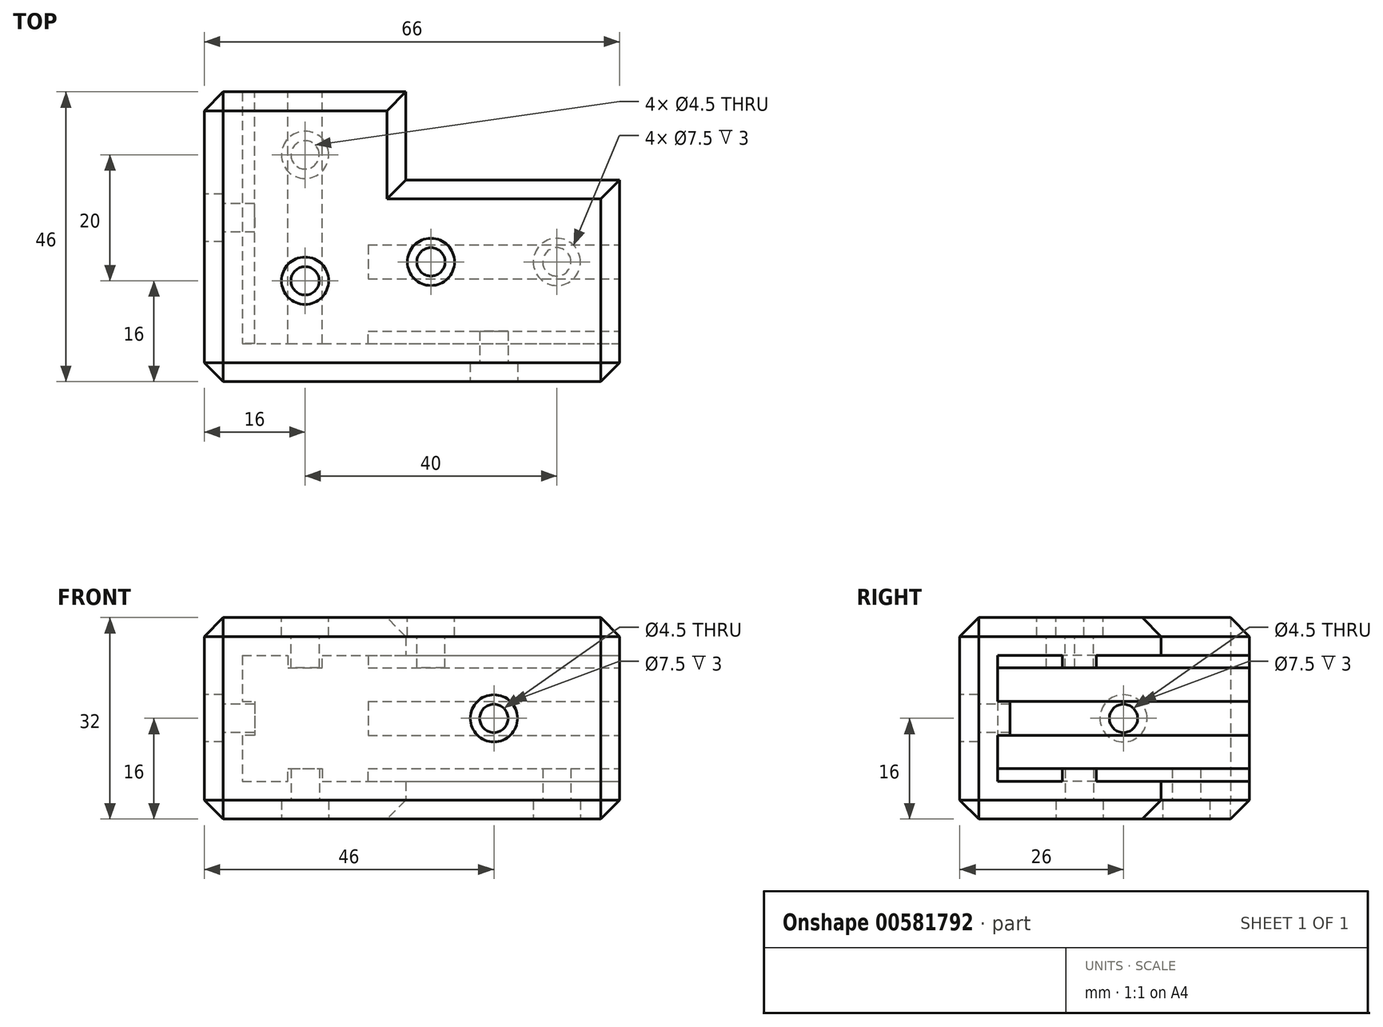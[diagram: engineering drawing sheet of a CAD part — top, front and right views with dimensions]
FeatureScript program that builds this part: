
annotation { "Feature Type Name" : "Feature", "Feature Type Description" : "" }
export const myFeature = defineFeature(function(context is Context, id is Id, definition is map)
    precondition{}
    {
        {
            var Q0;
            Q0=qCreatedBy(makeId("Top.planeOp"),FACE);
            var sketch = newSketch(context, id + "F0", { "sketchPlane" : qUnion([Q0])});
            skLineSegment(sketch, "E0", {"start": v(20, 40) * mm, "end": v(20, 20) * mm, "construction": true});
            skLineSegment(sketch, "E1", {"start": v(20, 20) * mm, "end": v(60, 20) * mm, "construction": true});
            skLineSegment(sketch, "E2", {"start": v(60, 20) * mm, "end": v(60, 0) * mm, "construction": true});
            skLineSegment(sketch, "E3", {"start": v(60, 0) * mm, "end": v(0, 0) * mm, "construction": true});
            skLineSegment(sketch, "E4", {"start": v(0, 0) * mm, "end": v(0, 40) * mm, "construction": true});
            skLineSegment(sketch, "E5", {"start": v(0, 40) * mm, "end": v(20, 40) * mm, "construction": true});
            skLineSegment(sketch, "E6", {"start": v(3.86, 40) * mm, "end": v(26, 40) * mm});
            skLineSegment(sketch, "E7", {"start": v(26, 40) * mm, "end": v(26, 26) * mm});
            skLineSegment(sketch, "E8", {"start": v(26, 26) * mm, "end": v(60, 26) * mm});
            skLineSegment(sketch, "E9", {"start": v(60, 26) * mm, "end": v(60, -6) * mm});
            skLineSegment(sketch, "E10", {"start": v(60, -6) * mm, "end": v(-6, -6) * mm});
            skLineSegment(sketch, "E11", {"start": v(-6, -6) * mm, "end": v(-6, 40) * mm});
            skLineSegment(sketch, "E12", {"start": v(-6, 40) * mm, "end": v(3.86, 40) * mm});
            skSolve(sketch);
        }
        {
            var Q0;
            Q0=qSketchRegion(id+"F0",true);
            extrude(context, id + "F1", {"entities" : qUnion([Q0]), "depth" : 6 * mm});
        }
        {
            var Q0;
            Q0=makeQuery(id+"F1.opExtrude","CAP_FACE",FACE,{"disambiguationData":[OSD([sQuery(id+"F0.wireOp",EDGE,"E6"),sQuery(id+"F0.wireOp",EDGE,"E7"),sQuery(id+"F0.wireOp",EDGE,"E8"),sQuery(id+"F0.wireOp",EDGE,"E9"),sQuery(id+"F0.wireOp",EDGE,"E10"),sQuery(id+"F0.wireOp",EDGE,"E11"),sQuery(id+"F0.wireOp",EDGE,"E12")])],"isStart":false});
            var sketch = newSketch(context, id + "F2", { "sketchPlane" : qUnion([Q0])});
            skLineSegment(sketch, "E13", {"start": v(-6, 40) * mm, "end": v(0, 40) * mm});
            skLineSegment(sketch, "E14", {"start": v(0, 40) * mm, "end": v(0, 0) * mm});
            skLineSegment(sketch, "E15", {"start": v(0, 0) * mm, "end": v(60, 0) * mm});
            skLineSegment(sketch, "E16", {"start": v(60, 0) * mm, "end": v(60, -6) * mm});
            skLineSegment(sketch, "E17", {"start": v(60, -6) * mm, "end": v(-6, -6) * mm});
            skLineSegment(sketch, "E18", {"start": v(-6, -6) * mm, "end": v(-6, 40) * mm});
            skSolve(sketch);
        }
        {
            var Q0;
            Q0=qSketchRegion(id+"F2",true);
            extrude(context, id + "F3", {"entities" : qUnion([Q0]), "operationType" : NewBodyOperationType.ADD, "depth" : 20 * mm});
        }
        {
            var Q0;
            Q0=makeQuery(id+"F3.opExtrude","CAP_FACE",FACE,{"disambiguationData":[OSD([sQuery(id+"F2.wireOp",EDGE,"E13"),sQuery(id+"F2.wireOp",EDGE,"E14"),sQuery(id+"F2.wireOp",EDGE,"E15"),sQuery(id+"F2.wireOp",EDGE,"E16"),sQuery(id+"F2.wireOp",EDGE,"E17"),sQuery(id+"F2.wireOp",EDGE,"E18")])],"isStart":false});
            var sketch = newSketch(context, id + "F4", { "sketchPlane" : qUnion([Q0])});
            skLineSegment(sketch, "E19", {"start": v(-6, -6) * mm, "end": v(-6, 40) * mm});
            skLineSegment(sketch, "E20", {"start": v(-6, 40) * mm, "end": v(26, 40) * mm});
            skLineSegment(sketch, "E21", {"start": v(26, 40) * mm, "end": v(26, 26) * mm});
            skLineSegment(sketch, "E22", {"start": v(26, 26) * mm, "end": v(60, 26) * mm});
            skLineSegment(sketch, "E23", {"start": v(60, 26) * mm, "end": v(60, -6) * mm});
            skLineSegment(sketch, "E24", {"start": v(60, -6) * mm, "end": v(-6, -6) * mm});
            skSolve(sketch);
        }
        {
            var Q0;
            Q0=qSketchRegion(id+"F4",true);
            extrude(context, id + "F5", {"entities" : qUnion([Q0]), "operationType" : NewBodyOperationType.ADD, "depth" : 6 * mm});
        }
        {
            var Q0;
            Q0=makeQuery(id+"F5.boolean.opBoolean","MERGE",FACE,{"derivedFrom":[makeQuery(id+"F3.boolean.opBoolean","MERGE",FACE,{"derivedFrom":[makeQuery(id+"F1.opExtrude","SWEPT_FACE",FACE,{"disambiguationData":[OSD([sQuery(id+"F0.wireOp",EDGE,"E9")])]}),makeQuery(id+"F3.opExtrude","SWEPT_FACE",FACE,{"disambiguationData":[OSD([sQuery(id+"F2.wireOp",EDGE,"E16")])]})]}),makeQuery(id+"F5.opExtrude","SWEPT_FACE",FACE,{"disambiguationData":[OSD([sQuery(id+"F4.wireOp",EDGE,"E23")])]})]});
            var sketch = newSketch(context, id + "F6", { "sketchPlane" : qUnion([Q0])});
            skLineSegment(sketch, "E25", {"start": v(13, 26) * mm, "end": v(10.29, 26) * mm});
            skLineSegment(sketch, "E26", {"start": v(10.29, 26) * mm, "end": v(10.29, 24) * mm});
            skLineSegment(sketch, "E27", {"start": v(10.29, 24) * mm, "end": v(15.7, 24) * mm});
            skLineSegment(sketch, "E28", {"start": v(15.7, 24) * mm, "end": v(15.7, 26) * mm});
            skLineSegment(sketch, "E29", {"start": v(15.7, 26) * mm, "end": v(13, 26) * mm});
            skLineSegment(sketch, "E30", {"start": v(13, 6) * mm, "end": v(10.29, 6) * mm});
            skLineSegment(sketch, "E31", {"start": v(10.29, 6) * mm, "end": v(10.29, 8) * mm});
            skLineSegment(sketch, "E32", {"start": v(10.29, 8) * mm, "end": v(15.7, 8) * mm});
            skLineSegment(sketch, "E33", {"start": v(15.7, 8) * mm, "end": v(15.7, 6) * mm});
            skLineSegment(sketch, "E34", {"start": v(15.7, 6) * mm, "end": v(13, 6) * mm});
            skLineSegment(sketch, "E35", {"start": v(0, 16) * mm, "end": v(0, 18.7) * mm});
            skLineSegment(sketch, "E36", {"start": v(0, 18.7) * mm, "end": v(2, 18.7) * mm});
            skLineSegment(sketch, "E37", {"start": v(2, 18.7) * mm, "end": v(2, 13.29) * mm});
            skLineSegment(sketch, "E38", {"start": v(2, 13.29) * mm, "end": v(0, 13.29) * mm});
            skLineSegment(sketch, "E39", {"start": v(0, 13.29) * mm, "end": v(0, 16) * mm});
            skSolve(sketch);
        }
        {
            var Q0;
            Q0=qSketchRegion(id+"F6",true);
            extrude(context, id + "F7", {"entities" : qUnion([Q0]), "operationType" : NewBodyOperationType.ADD, "oppositeDirection" : true, "depth" : 40 * mm});
        }
        {
            var Q0;
            Q0=makeQuery(id+"F5.boolean.opBoolean","MERGE",FACE,{"derivedFrom":[makeQuery(id+"F3.boolean.opBoolean","MERGE",FACE,{"derivedFrom":[makeQuery(id+"F1.opExtrude","SWEPT_FACE",FACE,{"disambiguationData":[OSD([sQuery(id+"F0.wireOp",EDGE,"E6"),sQuery(id+"F0.wireOp",EDGE,"E12")])]}),makeQuery(id+"F3.opExtrude","SWEPT_FACE",FACE,{"disambiguationData":[OSD([sQuery(id+"F2.wireOp",EDGE,"E13")])]})]}),makeQuery(id+"F5.opExtrude","SWEPT_FACE",FACE,{"disambiguationData":[OSD([sQuery(id+"F4.wireOp",EDGE,"E20")])]})]});
            var sketch = newSketch(context, id + "F8", { "sketchPlane" : qUnion([Q0])});
            skLineSegment(sketch, "E40", {"start": v(0, 16) * mm, "end": v(0, 18.71) * mm});
            skLineSegment(sketch, "E41", {"start": v(0, 18.71) * mm, "end": v(-2, 18.71) * mm});
            skLineSegment(sketch, "E42", {"start": v(-2, 18.71) * mm, "end": v(-2, 13.29) * mm});
            skLineSegment(sketch, "E43", {"start": v(-2, 13.29) * mm, "end": v(0, 13.29) * mm});
            skLineSegment(sketch, "E44", {"start": v(0, 13.29) * mm, "end": v(0, 16) * mm});
            skLineSegment(sketch, "E45", {"start": v(-10, 26) * mm, "end": v(-12.7, 26) * mm});
            skLineSegment(sketch, "E46", {"start": v(-7.3, 26) * mm, "end": v(-10, 26) * mm});
            skLineSegment(sketch, "E47", {"start": v(-10, 6) * mm, "end": v(-7.29, 6) * mm});
            skLineSegment(sketch, "E48", {"start": v(-7.29, 6) * mm, "end": v(-7.29, 8) * mm});
            skLineSegment(sketch, "E49", {"start": v(-7.29, 8) * mm, "end": v(-12.7, 8) * mm});
            skLineSegment(sketch, "E50", {"start": v(-12.7, 8) * mm, "end": v(-12.71, 6) * mm});
            skLineSegment(sketch, "E51", {"start": v(-12.7, 6) * mm, "end": v(-10, 6) * mm});
            skLineSegment(sketch, "E52", {"start": v(-7.3, 26) * mm, "end": v(-7.3, 24) * mm});
            skLineSegment(sketch, "E53", {"start": v(-7.3, 24) * mm, "end": v(-12.71, 24) * mm});
            skLineSegment(sketch, "E54", {"start": v(-12.71, 24) * mm, "end": v(-12.71, 26) * mm});
            skSolve(sketch);
        }
        {
            var Q0;
            Q0=qSketchRegion(id+"F8",true);
            extrude(context, id + "F9", {"entities" : qUnion([Q0]), "operationType" : NewBodyOperationType.ADD, "oppositeDirection" : true, "depth" : 40 * mm});
        }
        {
            var Q0;
            Q0=makeQuery(id+"F1.opExtrude","CAP_FACE",FACE,{"disambiguationData":[OSD([sQuery(id+"F0.wireOp",EDGE,"E6"),sQuery(id+"F0.wireOp",EDGE,"E7"),sQuery(id+"F0.wireOp",EDGE,"E8"),sQuery(id+"F0.wireOp",EDGE,"E9"),sQuery(id+"F0.wireOp",EDGE,"E10"),sQuery(id+"F0.wireOp",EDGE,"E11"),sQuery(id+"F0.wireOp",EDGE,"E12")])],"isStart":true});
            var sketch = newSketch(context, id + "F10", { "sketchPlane" : qUnion([Q0])});
            skCircle(sketch, "E55", {"center": v(50, -13) * mm, "radius": 2.25 * mm});
            skCircle(sketch, "E56", {"center": v(10, -30) * mm, "radius": 2.25 * mm});
            skSolve(sketch);
        }
        {
            var Q0;
            Q0=qSketchRegion(id+"F10",true);
            extrude(context, id + "F11", {"entities" : qUnion([Q0]), "operationType" : NewBodyOperationType.REMOVE, "endBound" : BoundingType.UP_TO_NEXT, "oppositeDirection" : true, "depth" : 25 * mm});
        }
        {
            var Q0;
            Q0=makeQuery(id+"F5.opExtrude","CAP_FACE",FACE,{"disambiguationData":[OSD([sQuery(id+"F4.wireOp",EDGE,"E19"),sQuery(id+"F4.wireOp",EDGE,"E20"),sQuery(id+"F4.wireOp",EDGE,"E21"),sQuery(id+"F4.wireOp",EDGE,"E22"),sQuery(id+"F4.wireOp",EDGE,"E23"),sQuery(id+"F4.wireOp",EDGE,"E24")])],"isStart":false});
            var sketch = newSketch(context, id + "F12", { "sketchPlane" : qUnion([Q0])});
            skCircle(sketch, "E57", {"center": v(10, 10) * mm, "radius": 2.25 * mm});
            skCircle(sketch, "E58", {"center": v(30, 13) * mm, "radius": 2.25 * mm});
            skSolve(sketch);
        }
        {
            var Q0;
            Q0=qSketchRegion(id+"F12",true);
            extrude(context, id + "F13", {"entities" : qUnion([Q0]), "operationType" : NewBodyOperationType.REMOVE, "endBound" : BoundingType.UP_TO_NEXT, "oppositeDirection" : true, "depth" : 25 * mm});
        }
        {
            var Q0;
            Q0=makeQuery(id+"F5.boolean.opBoolean","MERGE",FACE,{"derivedFrom":[makeQuery(id+"F3.boolean.opBoolean","MERGE",FACE,{"derivedFrom":[makeQuery(id+"F1.opExtrude","SWEPT_FACE",FACE,{"disambiguationData":[OSD([sQuery(id+"F0.wireOp",EDGE,"E10")])]}),makeQuery(id+"F3.opExtrude","SWEPT_FACE",FACE,{"disambiguationData":[OSD([sQuery(id+"F2.wireOp",EDGE,"E17")])]})]}),makeQuery(id+"F5.opExtrude","SWEPT_FACE",FACE,{"disambiguationData":[OSD([sQuery(id+"F4.wireOp",EDGE,"E24")])]})]});
            var sketch = newSketch(context, id + "F14", { "sketchPlane" : qUnion([Q0])});
            skCircle(sketch, "E59", {"center": v(40, 16) * mm, "radius": 2.25 * mm});
            skSolve(sketch);
        }
        {
            var Q0;
            Q0=qSketchRegion(id+"F14",true);
            extrude(context, id + "F15", {"entities" : qUnion([Q0]), "operationType" : NewBodyOperationType.REMOVE, "endBound" : BoundingType.UP_TO_NEXT, "oppositeDirection" : true, "depth" : 25 * mm});
        }
        {
            var Q0;
            Q0=makeQuery(id+"F5.boolean.opBoolean","MERGE",FACE,{"derivedFrom":[makeQuery(id+"F3.boolean.opBoolean","MERGE",FACE,{"derivedFrom":[makeQuery(id+"F1.opExtrude","SWEPT_FACE",FACE,{"disambiguationData":[OSD([sQuery(id+"F0.wireOp",EDGE,"E11")])]}),makeQuery(id+"F3.opExtrude","SWEPT_FACE",FACE,{"disambiguationData":[OSD([sQuery(id+"F2.wireOp",EDGE,"E18")])]})]}),makeQuery(id+"F5.opExtrude","SWEPT_FACE",FACE,{"disambiguationData":[OSD([sQuery(id+"F4.wireOp",EDGE,"E19")])]})]});
            var sketch = newSketch(context, id + "F16", { "sketchPlane" : qUnion([Q0])});
            skCircle(sketch, "E60", {"center": v(-20, 16) * mm, "radius": 2.25 * mm});
            skSolve(sketch);
        }
        {
            var Q0;
            Q0=qSketchRegion(id+"F16",true);
            extrude(context, id + "F17", {"entities" : qUnion([Q0]), "operationType" : NewBodyOperationType.REMOVE, "endBound" : BoundingType.UP_TO_NEXT, "oppositeDirection" : true, "depth" : 25 * mm});
        }
        {
            var Q0;
            Q0=makeQuery(id+"F5.opExtrude","CAP_FACE",FACE,{"disambiguationData":[OSD([sQuery(id+"F4.wireOp",EDGE,"E19"),sQuery(id+"F4.wireOp",EDGE,"E20"),sQuery(id+"F4.wireOp",EDGE,"E21"),sQuery(id+"F4.wireOp",EDGE,"E22"),sQuery(id+"F4.wireOp",EDGE,"E23"),sQuery(id+"F4.wireOp",EDGE,"E24")])],"isStart":false});
            var sketch = newSketch(context, id + "F18", { "sketchPlane" : qUnion([Q0])});
            skCircle(sketch, "E61", {"center": v(10, 10) * mm, "radius": 3.75 * mm});
            skCircle(sketch, "E62", {"center": v(30, 13) * mm, "radius": 3.75 * mm});
            skSolve(sketch);
        }
        {
            var Q0;
            Q0=qSketchRegion(id+"F18",true);
            extrude(context, id + "F19", {"entities" : qUnion([Q0]), "operationType" : NewBodyOperationType.REMOVE, "oppositeDirection" : true, "depth" : 3 * mm});
        }
        {
            var Q0;
            Q0=makeQuery(id+"F5.boolean.opBoolean","MERGE",FACE,{"derivedFrom":[makeQuery(id+"F3.boolean.opBoolean","MERGE",FACE,{"derivedFrom":[makeQuery(id+"F1.opExtrude","SWEPT_FACE",FACE,{"disambiguationData":[OSD([sQuery(id+"F0.wireOp",EDGE,"E11")])]}),makeQuery(id+"F3.opExtrude","SWEPT_FACE",FACE,{"disambiguationData":[OSD([sQuery(id+"F2.wireOp",EDGE,"E18")])]})]}),makeQuery(id+"F5.opExtrude","SWEPT_FACE",FACE,{"disambiguationData":[OSD([sQuery(id+"F4.wireOp",EDGE,"E19")])]})]});
            var sketch = newSketch(context, id + "F20", { "sketchPlane" : qUnion([Q0])});
            skCircle(sketch, "E63", {"center": v(-20, 16) * mm, "radius": 3.75 * mm});
            skSolve(sketch);
        }
        {
            var Q0;
            Q0=qSketchRegion(id+"F20",true);
            extrude(context, id + "F21", {"entities" : qUnion([Q0]), "operationType" : NewBodyOperationType.REMOVE, "oppositeDirection" : true, "depth" : 3 * mm});
        }
        {
            var Q0;
            Q0=makeQuery(id+"F1.opExtrude","CAP_FACE",FACE,{"disambiguationData":[OSD([sQuery(id+"F0.wireOp",EDGE,"E6"),sQuery(id+"F0.wireOp",EDGE,"E7"),sQuery(id+"F0.wireOp",EDGE,"E8"),sQuery(id+"F0.wireOp",EDGE,"E9"),sQuery(id+"F0.wireOp",EDGE,"E10"),sQuery(id+"F0.wireOp",EDGE,"E11"),sQuery(id+"F0.wireOp",EDGE,"E12")])],"isStart":true});
            var sketch = newSketch(context, id + "F22", { "sketchPlane" : qUnion([Q0])});
            skCircle(sketch, "E64", {"center": v(10, -30) * mm, "radius": 3.75 * mm});
            skCircle(sketch, "E65", {"center": v(50, -13) * mm, "radius": 3.75 * mm});
            skSolve(sketch);
        }
        {
            var Q0;
            Q0=qSketchRegion(id+"F22",true);
            extrude(context, id + "F23", {"entities" : qUnion([Q0]), "operationType" : NewBodyOperationType.REMOVE, "oppositeDirection" : true, "depth" : 3 * mm});
        }
        {
            var Q0;
            Q0=makeQuery(id+"F5.boolean.opBoolean","MERGE",FACE,{"derivedFrom":[makeQuery(id+"F3.boolean.opBoolean","MERGE",FACE,{"derivedFrom":[makeQuery(id+"F1.opExtrude","SWEPT_FACE",FACE,{"disambiguationData":[OSD([sQuery(id+"F0.wireOp",EDGE,"E10")])]}),makeQuery(id+"F3.opExtrude","SWEPT_FACE",FACE,{"disambiguationData":[OSD([sQuery(id+"F2.wireOp",EDGE,"E17")])]})]}),makeQuery(id+"F5.opExtrude","SWEPT_FACE",FACE,{"disambiguationData":[OSD([sQuery(id+"F4.wireOp",EDGE,"E24")])]})]});
            var sketch = newSketch(context, id + "F24", { "sketchPlane" : qUnion([Q0])});
            skCircle(sketch, "E66", {"center": v(40, 16) * mm, "radius": 3.75 * mm});
            skSolve(sketch);
        }
        {
            var Q0;
            Q0=qSketchRegion(id+"F24",true);
            extrude(context, id + "F25", {"entities" : qUnion([Q0]), "operationType" : NewBodyOperationType.REMOVE, "oppositeDirection" : true, "depth" : 3 * mm});
        }
        {
            var Q0;
            Q0=makeQuery(id+"F1.opExtrude","CAP_EDGE",EDGE,{"disambiguationData":[OSD([sQuery(id+"F0.wireOp",EDGE,"E10")])],"isStart":true});
            var Q1;
            Q1=makeQuery(id+"F1.opExtrude","CAP_EDGE",EDGE,{"disambiguationData":[OSD([sQuery(id+"F0.wireOp",EDGE,"E8")])],"isStart":true});
            var Q2;
            Q2=makeQuery(id+"F1.opExtrude","CAP_EDGE",EDGE,{"disambiguationData":[OSD([sQuery(id+"F0.wireOp",EDGE,"E7")])],"isStart":true});
            var Q3;
            Q3=makeQuery(id+"F1.opExtrude","CAP_EDGE",EDGE,{"disambiguationData":[OSD([sQuery(id+"F0.wireOp",EDGE,"E6"),sQuery(id+"F0.wireOp",EDGE,"E12")])],"isStart":true});
            var Q4;
            Q4=makeQuery(id+"F1.opExtrude","CAP_EDGE",EDGE,{"disambiguationData":[OSD([sQuery(id+"F0.wireOp",EDGE,"E11")])],"isStart":true});
            var Q5;
            Q5=makeQuery(id+"F5.boolean.opBoolean","MERGE",EDGE,{"derivedFrom":[makeQuery(id+"F3.boolean.opBoolean","MERGE",EDGE,{"derivedFrom":[makeQuery(id+"F1.opExtrude","SWEPT_EDGE",EDGE,{"disambiguationData":[OSD([sQuery(id+"F0.wireOp",EDGE,"E10"),sQuery(id+"F0.wireOp",EDGE,"E11")])]}),makeQuery(id+"F3.opExtrude","SWEPT_EDGE",EDGE,{"disambiguationData":[OSD([sQuery(id+"F2.wireOp",EDGE,"E17"),sQuery(id+"F2.wireOp",EDGE,"E18")])]})]}),makeQuery(id+"F5.opExtrude","SWEPT_EDGE",EDGE,{"disambiguationData":[OSD([sQuery(id+"F4.wireOp",EDGE,"E19"),sQuery(id+"F4.wireOp",EDGE,"E24")])]})]});
            var Q6;
            Q6=makeQuery(id+"F5.opExtrude","CAP_EDGE",EDGE,{"disambiguationData":[OSD([sQuery(id+"F4.wireOp",EDGE,"E24")])],"isStart":false});
            var Q7;
            Q7=makeQuery(id+"F5.opExtrude","CAP_EDGE",EDGE,{"disambiguationData":[OSD([sQuery(id+"F4.wireOp",EDGE,"E19")])],"isStart":false});
            var Q8;
            Q8=makeQuery(id+"F5.opExtrude","CAP_EDGE",EDGE,{"disambiguationData":[OSD([sQuery(id+"F4.wireOp",EDGE,"E20")])],"isStart":false});
            var Q9;
            Q9=makeQuery(id+"F5.opExtrude","CAP_EDGE",EDGE,{"disambiguationData":[OSD([sQuery(id+"F4.wireOp",EDGE,"E21")])],"isStart":false});
            var Q10;
            Q10=makeQuery(id+"F5.opExtrude","CAP_EDGE",EDGE,{"disambiguationData":[OSD([sQuery(id+"F4.wireOp",EDGE,"E22")])],"isStart":false});
            var Q11;
            Q11=makeQuery(id+"F5.opExtrude","CAP_EDGE",EDGE,{"disambiguationData":[OSD([sQuery(id+"F4.wireOp",EDGE,"E23")])],"isStart":false});
            var Q12;
            Q12=makeQuery(id+"F1.opExtrude","CAP_EDGE",EDGE,{"disambiguationData":[OSD([sQuery(id+"F0.wireOp",EDGE,"E9")])],"isStart":true});
            var Q13;
            Q13=makeQuery(id+"F5.boolean.opBoolean","MERGE",EDGE,{"derivedFrom":[makeQuery(id+"F3.boolean.opBoolean","MERGE",EDGE,{"derivedFrom":[makeQuery(id+"F1.opExtrude","SWEPT_EDGE",EDGE,{"disambiguationData":[OSD([sQuery(id+"F0.wireOp",EDGE,"E11"),sQuery(id+"F0.wireOp",EDGE,"E12")])]}),makeQuery(id+"F3.opExtrude","SWEPT_EDGE",EDGE,{"disambiguationData":[OSD([sQuery(id+"F2.wireOp",EDGE,"E13"),sQuery(id+"F2.wireOp",EDGE,"E18")])]})]}),makeQuery(id+"F5.opExtrude","SWEPT_EDGE",EDGE,{"disambiguationData":[OSD([sQuery(id+"F4.wireOp",EDGE,"E19"),sQuery(id+"F4.wireOp",EDGE,"E20")])]})]});
            var Q14;
            Q14=makeQuery(id+"F5.boolean.opBoolean","MERGE",EDGE,{"derivedFrom":[makeQuery(id+"F3.boolean.opBoolean","MERGE",EDGE,{"derivedFrom":[makeQuery(id+"F1.opExtrude","SWEPT_EDGE",EDGE,{"disambiguationData":[OSD([sQuery(id+"F0.wireOp",EDGE,"E9"),sQuery(id+"F0.wireOp",EDGE,"E10")])]}),makeQuery(id+"F3.opExtrude","SWEPT_EDGE",EDGE,{"disambiguationData":[OSD([sQuery(id+"F2.wireOp",EDGE,"E16"),sQuery(id+"F2.wireOp",EDGE,"E17")])]})]}),makeQuery(id+"F5.opExtrude","SWEPT_EDGE",EDGE,{"disambiguationData":[OSD([sQuery(id+"F4.wireOp",EDGE,"E23"),sQuery(id+"F4.wireOp",EDGE,"E24")])]})]});
            chamfer(context, id + "F26", {"entities" : qUnion([Q0, Q1, Q2, Q3, Q4, Q5, Q6, Q7, Q8, Q9, Q10, Q11, Q12, Q13, Q14]), "width" : 3 * mm, "tangentPropagation" : true});
        }
    });
